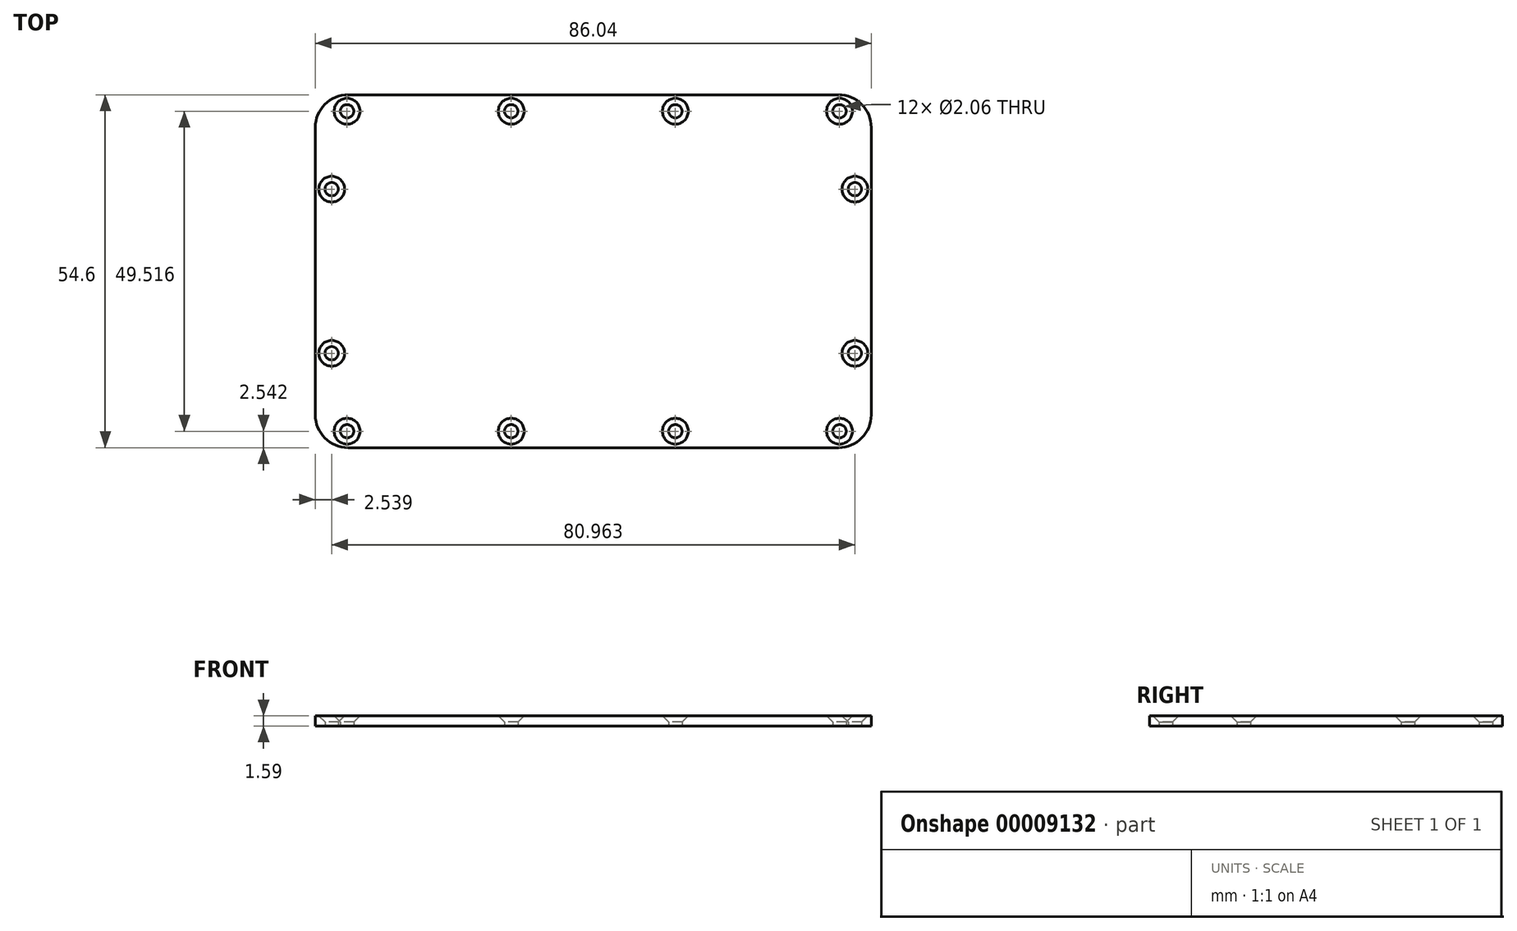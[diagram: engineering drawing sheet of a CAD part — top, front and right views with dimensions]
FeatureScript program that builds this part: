
annotation { "Feature Type Name" : "Feature", "Feature Type Description" : "" }
export const myFeature = defineFeature(function(context is Context, id is Id, definition is map)
    precondition{}
    {
        {
            var Q0;
            Q0=qCreatedBy(makeId("Top.planeOp"),FACE);
            var sketch = newSketch(context, id + "F0", { "sketchPlane" : qUnion([Q0])});
            skLineSegment(sketch, "E0.bottom", {"start": v(-43.02, 27.3) * mm, "end": v(43.02, 27.3) * mm});
            skLineSegment(sketch, "E0.top", {"start": v(-43.02, -27.3) * mm, "end": v(43.02, -27.3) * mm});
            skLineSegment(sketch, "E0.left", {"start": v(-43.02, 27.3) * mm, "end": v(-43.02, -27.3) * mm});
            skLineSegment(sketch, "E0.right", {"start": v(43.02, 27.3) * mm, "end": v(43.02, -27.3) * mm});
            skLineSegment(sketch, "E1", {"start": v(0, 28.85) * mm, "end": v(0, -30.48) * mm, "construction": true});
            skLineSegment(sketch, "E2", {"start": v(-35.92, 0) * mm, "end": v(38.92, 0) * mm, "construction": true});
            skCircle(sketch, "E3", {"center": v(-38.1, 24.76) * mm, "radius": 1.03 * mm});
            skCircle(sketch, "E4.0.MirrorC", {"center": v(-38.1, -24.76) * mm, "radius": 1.03 * mm});
            skCircle(sketch, "E5.1.0.0", {"center": v(-12.7, 24.76) * mm, "radius": 1.03 * mm});
            skCircle(sketch, "E5.2.0.0", {"center": v(12.7, 24.76) * mm, "radius": 1.03 * mm});
            skCircle(sketch, "E5.3.0.0", {"center": v(38.1, 24.76) * mm, "radius": 1.03 * mm});
            skLineSegment(sketch, "E5.direction1", {"start": v(-38.1, 24.76) * mm, "end": v(-12.7, 24.76) * mm, "construction": true});
            skCircle(sketch, "E6.1.0.0", {"center": v(-12.7, -24.76) * mm, "radius": 1.03 * mm});
            skCircle(sketch, "E6.2.0.0", {"center": v(12.7, -24.76) * mm, "radius": 1.03 * mm});
            skCircle(sketch, "E6.3.0.0", {"center": v(38.1, -24.76) * mm, "radius": 1.03 * mm});
            skLineSegment(sketch, "E6.direction1", {"start": v(-38.1, -24.76) * mm, "end": v(-12.7, -24.76) * mm, "construction": true});
            skCircle(sketch, "E7", {"center": v(-40.48, 12.7) * mm, "radius": 1.03 * mm});
            skCircle(sketch, "E8.0.1.0", {"center": v(-40.48, -12.7) * mm, "radius": 1.03 * mm});
            skLineSegment(sketch, "E8.direction1", {"start": v(-40.48, 12.7) * mm, "end": v(-21.14, 12.74) * mm, "construction": true});
            skLineSegment(sketch, "E8.direction2", {"start": v(-40.48, 12.7) * mm, "end": v(-40.48, -12.7) * mm, "construction": true});
            skCircle(sketch, "E9.0.MirrorC", {"center": v(40.48, -12.7) * mm, "radius": 1.03 * mm});
            skCircle(sketch, "E9.1.MirrorC", {"center": v(40.48, 12.7) * mm, "radius": 1.03 * mm});
            skSolve(sketch);
        }
        {
            var Q0;
            Q0=makeQuery(id+"F0.imprint","IMPRINT",FACE,{"disambiguationData":[TD([[makeQuery(id+"F0.imprint","IMPRINT",EDGE,{"derivedFrom":sQuery(id+"F0.wireOp",EDGE,"E0.bottom")}),-1.0]])]});
            extrude(context, id + "F1", {"entities" : qUnion([Q0]), "depth" : 1.59 * mm});
        }
        {
            var Q0;
            Q0=makeQuery(id+"F1.opExtrude","SWEPT_EDGE",EDGE,{"disambiguationData":[OSD([sQuery(id+"F0.wireOp",EDGE,"E0.bottom"),sQuery(id+"F0.wireOp",EDGE,"E0.left")])]});
            var Q1;
            Q1=makeQuery(id+"F1.opExtrude","SWEPT_EDGE",EDGE,{"disambiguationData":[OSD([sQuery(id+"F0.wireOp",EDGE,"E0.top"),sQuery(id+"F0.wireOp",EDGE,"E0.left")])]});
            var Q2;
            Q2=makeQuery(id+"F1.opExtrude","SWEPT_EDGE",EDGE,{"disambiguationData":[OSD([sQuery(id+"F0.wireOp",EDGE,"E0.top"),sQuery(id+"F0.wireOp",EDGE,"E0.right")])]});
            var Q3;
            Q3=makeQuery(id+"F1.opExtrude","SWEPT_EDGE",EDGE,{"disambiguationData":[OSD([sQuery(id+"F0.wireOp",EDGE,"E0.bottom"),sQuery(id+"F0.wireOp",EDGE,"E0.right")])]});
            fillet(context, id + "F2", {"entities" : qUnion([Q0, Q1, Q2, Q3]), "radius" : 5.08 * mm, "tangentPropagation" : true, "allowEdgeOverflow" : false});
        }
        {
            var Q0;
            Q0=makeQuery(id+"F1.opExtrude","CAP_EDGE",EDGE,{"disambiguationData":[OSD([sQuery(id+"F0.wireOp",EDGE,"E3")])],"isStart":false});
            var Q1;
            Q1=makeQuery(id+"F1.opExtrude","CAP_EDGE",EDGE,{"disambiguationData":[OSD([sQuery(id+"F0.wireOp",EDGE,"E5.1.0.0")])],"isStart":false});
            var Q2;
            Q2=makeQuery(id+"F1.opExtrude","CAP_EDGE",EDGE,{"disambiguationData":[OSD([sQuery(id+"F0.wireOp",EDGE,"E5.2.0.0")])],"isStart":false});
            var Q3;
            Q3=makeQuery(id+"F1.opExtrude","CAP_EDGE",EDGE,{"disambiguationData":[OSD([sQuery(id+"F0.wireOp",EDGE,"E5.3.0.0")])],"isStart":false});
            var Q4;
            Q4=makeQuery(id+"F1.opExtrude","CAP_EDGE",EDGE,{"disambiguationData":[OSD([sQuery(id+"F0.wireOp",EDGE,"E9.1.MirrorC")])],"isStart":false});
            var Q5;
            Q5=makeQuery(id+"F1.opExtrude","CAP_EDGE",EDGE,{"disambiguationData":[OSD([sQuery(id+"F0.wireOp",EDGE,"E9.0.MirrorC")])],"isStart":false});
            var Q6;
            Q6=makeQuery(id+"F1.opExtrude","CAP_EDGE",EDGE,{"disambiguationData":[OSD([sQuery(id+"F0.wireOp",EDGE,"E7")])],"isStart":false});
            var Q7;
            Q7=makeQuery(id+"F1.opExtrude","CAP_EDGE",EDGE,{"disambiguationData":[OSD([sQuery(id+"F0.wireOp",EDGE,"E8.0.1.0")])],"isStart":false});
            var Q8;
            Q8=makeQuery(id+"F1.opExtrude","CAP_EDGE",EDGE,{"disambiguationData":[OSD([sQuery(id+"F0.wireOp",EDGE,"E4.0.MirrorC")])],"isStart":false});
            var Q9;
            Q9=makeQuery(id+"F1.opExtrude","CAP_EDGE",EDGE,{"disambiguationData":[OSD([sQuery(id+"F0.wireOp",EDGE,"E6.1.0.0")])],"isStart":false});
            var Q10;
            Q10=makeQuery(id+"F1.opExtrude","CAP_EDGE",EDGE,{"disambiguationData":[OSD([sQuery(id+"F0.wireOp",EDGE,"E6.2.0.0")])],"isStart":false});
            var Q11;
            Q11=makeQuery(id+"F1.opExtrude","CAP_EDGE",EDGE,{"disambiguationData":[OSD([sQuery(id+"F0.wireOp",EDGE,"E6.3.0.0")])],"isStart":false});
            chamfer(context, id + "F3", {"entities" : qUnion([Q0, Q1, Q2, Q3, Q4, Q5, Q6, Q7, Q8, Q9, Q10, Q11]), "width" : 0.97 * mm, "tangentPropagation" : true});
        }
    });
